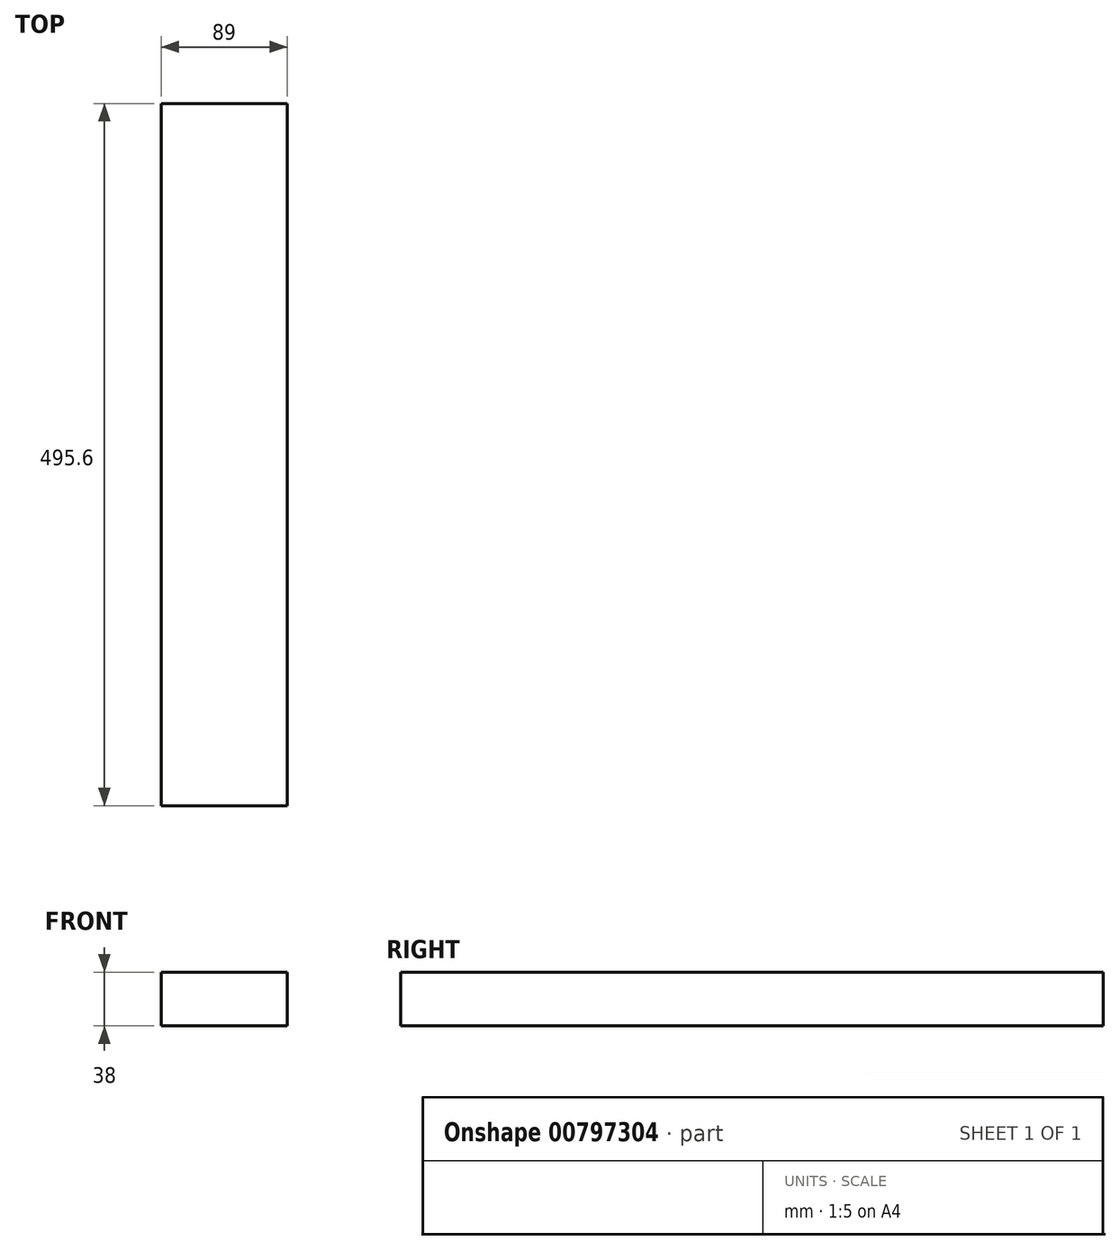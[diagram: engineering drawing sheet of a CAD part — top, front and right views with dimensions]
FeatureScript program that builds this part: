
annotation { "Feature Type Name" : "Feature", "Feature Type Description" : "" }
export const myFeature = defineFeature(function(context is Context, id is Id, definition is map)
    precondition{}
    {
        {
            var Q0;
            Q0=qCreatedBy(makeId("Front.planeOp"),FACE);
            var sketch = newSketch(context, id + "F0", { "sketchPlane" : qUnion([Q0])});
            skLineSegment(sketch, "E0.bottom", {"start": v(44.5, 19) * mm, "end": v(-44.5, 19) * mm});
            skLineSegment(sketch, "E0.top", {"start": v(44.5, -19) * mm, "end": v(-44.5, -19) * mm});
            skLineSegment(sketch, "E0.left", {"start": v(44.5, 19) * mm, "end": v(44.5, -19) * mm});
            skLineSegment(sketch, "E0.right", {"start": v(-44.5, 19) * mm, "end": v(-44.5, -19) * mm});
            skPoint(sketch, "E0.middle", {"position": v(0, 0) * mm});
            skSolve(sketch);
        }
        {
            var Q0;
            Q0=qSketchRegion(id+"F0",true);
            extrude(context, id + "F1", {"entities" : qUnion([Q0]), "depth" : 495.6 * mm, "offsetDistance" : 25 * mm, "symmetric" : true});
        }
    });
